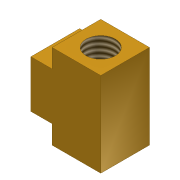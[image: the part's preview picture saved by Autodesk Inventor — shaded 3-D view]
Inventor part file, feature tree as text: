
AUTODESK INVENTOR PART (.ipt)
format: ipt  version: 2014 SP1 (Build 180222100, 222)  size: 114,176 bytes
history: native  units: mm (DEFAULTED — no unit token found)
features: extrude x4, sketch x4, thread x3, projected_geometry x3
ambient origin geometry x8: Origin, YZ Plane, XZ Plane, XY Plane, X Axis, Y Axis, Z Axis, Center Point
bodies: Solid1 (feature_tree)
feature tree (14):
  extrude  "Extrusion1"  Depth=14.605mm
  extrude  "Extrusion2"  Depth=14.224mm
  extrude  "Extrusion3"  Depth=6.35mm
  extrude  "Extrusion4"  Depth=13.7414mm
  thread  "Thread1"  [1 undecoded]
  thread  "Thread2"  [1 undecoded]
  thread  "Thread3"  [1 undecoded]
  sketch  "Sketch1"  dims[d0=14.605mm d1=14.605mm]
  sketch  "Sketch2"  dims[d2=25.4mm d3=0.0mm d4=14.224mm]
  projected_geometry  "Projected Loop1"
  sketch  "Sketch3"  dims[d5=6.35mm d6=0.0mm d7=8.763mm]
  projected_geometry  "Projected Loop2"
  sketch  "Sketch4"  dims[d8=6.35mm d9=0.0mm d10=8.763mm d11=13.7414mm d12=0.0mm d13=8.89mm d14=0.0mm d15=8.89mm d16=0.0mm d17=8.89mm d18=0.0mm]
  projected_geometry  "Projected Loop3"
note: 3 required parameter values undecoded (feature->parameter linkage not recoverable at this tier; creation-order binding heuristic only, values carry confidence <= 0.55)
